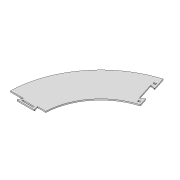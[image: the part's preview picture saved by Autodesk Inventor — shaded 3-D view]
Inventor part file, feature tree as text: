
AUTODESK INVENTOR PART (.ipt)
format: ipt  version: 2020 (Build 240168000, 168)  size: 263,680 bytes
history: native  units: mm
features: extrude x1, sketch x1
ambient origin geometry x8: Origin, YZ Plane, XZ Plane, XY Plane, X Axis, Y Axis, Z Axis, Center Point
bodies: Solid1 (feature_tree)
feature tree (2):
  extrude  "Extrusion1"  Depth=1.75mm
  sketch  "Sketch1"  dims[d0=504.787567mm d1=944.787567mm d34=1152.87mm d45=7.5mm d48=712.87mm d52=7.0mm d53=0.0mm d58=50.0mm d60=360.0deg d62=13.601997mm d63=25.0mm d65=50.0mm d71=50.0mm d72=7.5mm d74=3.5mm d75=3.5mm d79=0.0mm d80=8.0mm d81=1.75mm d83=50.0mm d84=8.0mm d85=1.75mm d86=50.0mm d88=360.0deg]
